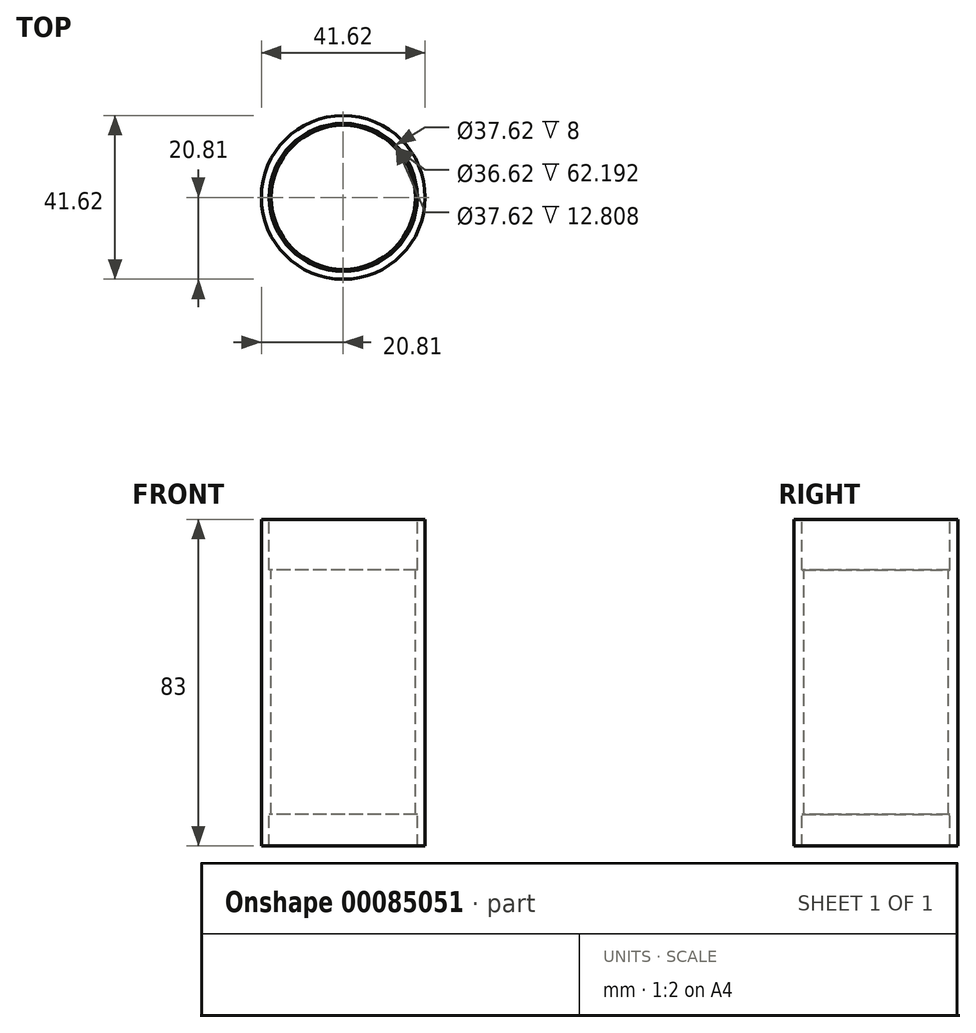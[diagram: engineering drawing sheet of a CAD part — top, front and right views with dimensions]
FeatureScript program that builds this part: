
annotation { "Feature Type Name" : "Feature", "Feature Type Description" : "" }
export const myFeature = defineFeature(function(context is Context, id is Id, definition is map)
    precondition{}
    {
        {
            var Q0;
            Q0=qCreatedBy(makeId("Front.planeOp"),FACE);
            var sketch = newSketch(context, id + "F0", { "sketchPlane" : qUnion([Q0])});
            skLineSegment(sketch, "E0", {"start": v(-20.8, 0) * mm, "end": v(-20.8, 83) * mm});
            skLineSegment(sketch, "E1", {"start": v(-20.8, 83) * mm, "end": v(-18.8, 83) * mm});
            skLineSegment(sketch, "E2", {"start": v(-18.8, 83) * mm, "end": v(-18.8, 70.2) * mm});
            skLineSegment(sketch, "E3", {"start": v(-18.8, 70.2) * mm, "end": v(-18.3, 70.2) * mm});
            skLineSegment(sketch, "E4", {"start": v(-18.3, 70.2) * mm, "end": v(-18.3, 8) * mm});
            skLineSegment(sketch, "E5", {"start": v(-18.3, 8) * mm, "end": v(-18.8, 8) * mm});
            skLineSegment(sketch, "E6", {"start": v(-18.8, 8) * mm, "end": v(-18.8, 0) * mm});
            skLineSegment(sketch, "E7", {"start": v(-18.8, 0) * mm, "end": v(-20.8, 0) * mm});
            skLineSegment(sketch, "E8", {"start": v(0, 72.6) * mm, "end": v(0, -27.38) * mm, "construction": true});
            skSolve(sketch);
        }
        {
            var Q0;
            Q0=makeQuery(id+"F0.imprint","IMPRINT",FACE,{"disambiguationData":[TD([[makeQuery(id+"F0.imprint","IMPRINT",EDGE,{"derivedFrom":sQuery(id+"F0.wireOp",EDGE,"E0")}),-1.0]])]});
            var Q1;
            Q1=sQuery(id+"F0.wireOp",EDGE,"E8");
            revolve(context, id + "F1", {"entities" : qUnion([Q0]), "axis" : qUnion([Q1]), "revolveType" : RevolveType.FULL});
        }
    });
